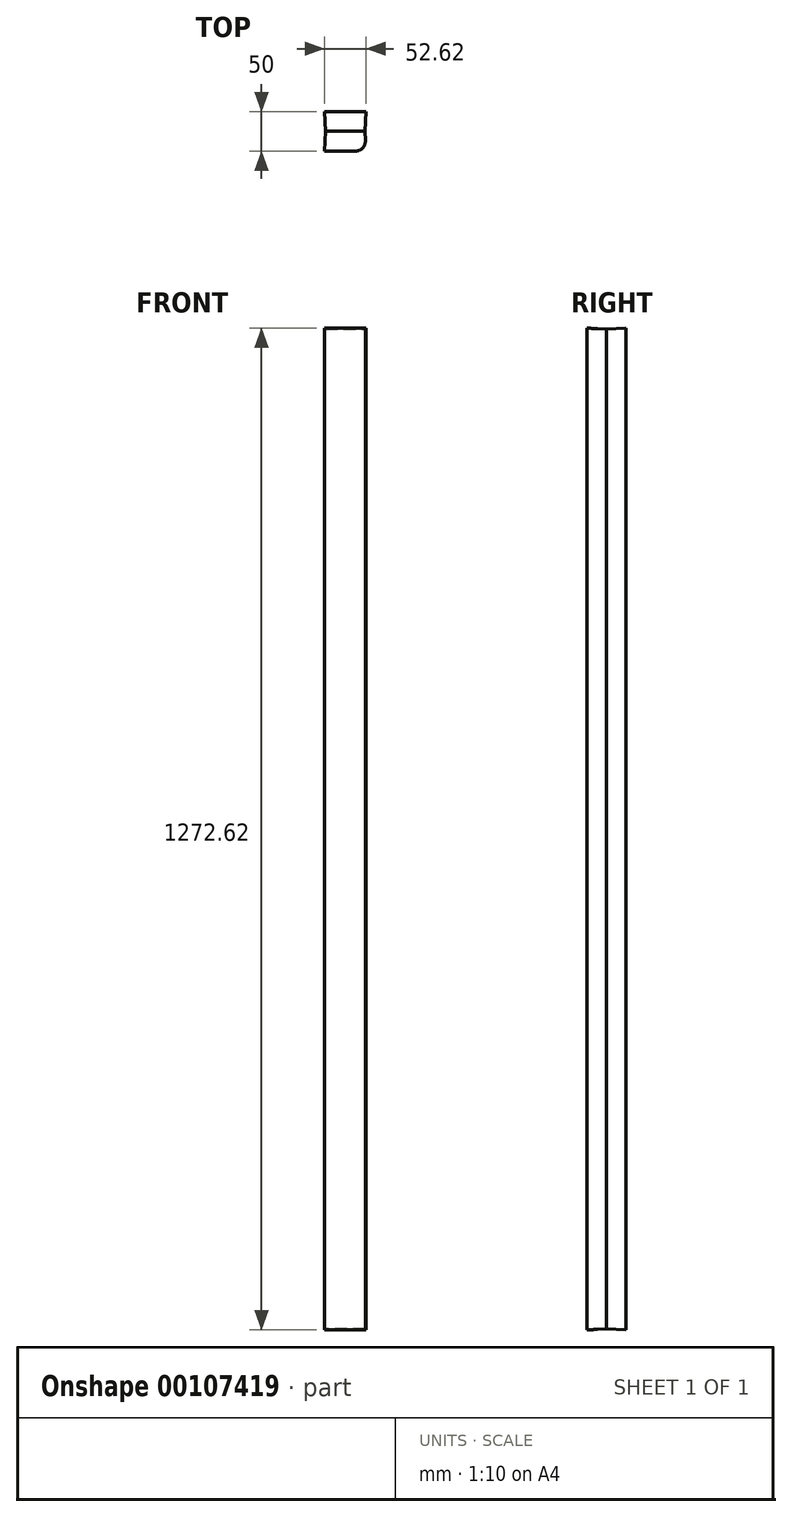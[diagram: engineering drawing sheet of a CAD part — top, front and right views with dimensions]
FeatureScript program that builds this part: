
annotation { "Feature Type Name" : "Feature", "Feature Type Description" : "" }
export const myFeature = defineFeature(function(context is Context, id is Id, definition is map)
    precondition{}
    {
        {
            var Q0;
            Q0=qCreatedBy(makeId("Front.planeOp"),FACE);
            var sketch = newSketch(context, id + "F0", { "sketchPlane" : qUnion([Q0])});
            skLineSegment(sketch, "E0.bottom", {"start": v(0, 0) * mm, "end": v(-50, 0) * mm});
            skLineSegment(sketch, "E0.top", {"start": v(0, 1270) * mm, "end": v(-50, 1270) * mm});
            skLineSegment(sketch, "E0.left", {"start": v(0, 0) * mm, "end": v(0, 1270) * mm});
            skLineSegment(sketch, "E0.right", {"start": v(-50, 0) * mm, "end": v(-50, 1270) * mm});
            skSolve(sketch);
        }
        {
            var Q0;
            Q0=makeQuery(id+"F0.imprint","IMPRINT",FACE,{"disambiguationData":[TD([[makeQuery(id+"F0.imprint","IMPRINT",EDGE,{"derivedFrom":sQuery(id+"F0.wireOp",EDGE,"E0.bottom")}),-1.0]])]});
            extrude(context, id + "F1", {"entities" : qUnion([Q0]), "endBound" : BoundingType.SYMMETRIC, "depth" : 50 * mm, "hasDraft" : true, "draftAngle" : 3 * degree});
        }
        {
            var Q0;
            Q0=makeQuery(id+"F1.opExtrude","CAP_EDGE",EDGE,{"disambiguationData":[OSD([sQuery(id+"F0.wireOp",EDGE,"E0.left")])],"isStart":false});
            fillet(context, id + "F2", {"entities" : qUnion([Q0]), "radius" : 12.7 * mm, "tangentPropagation" : true, "allowEdgeOverflow" : false});
        }
    });
